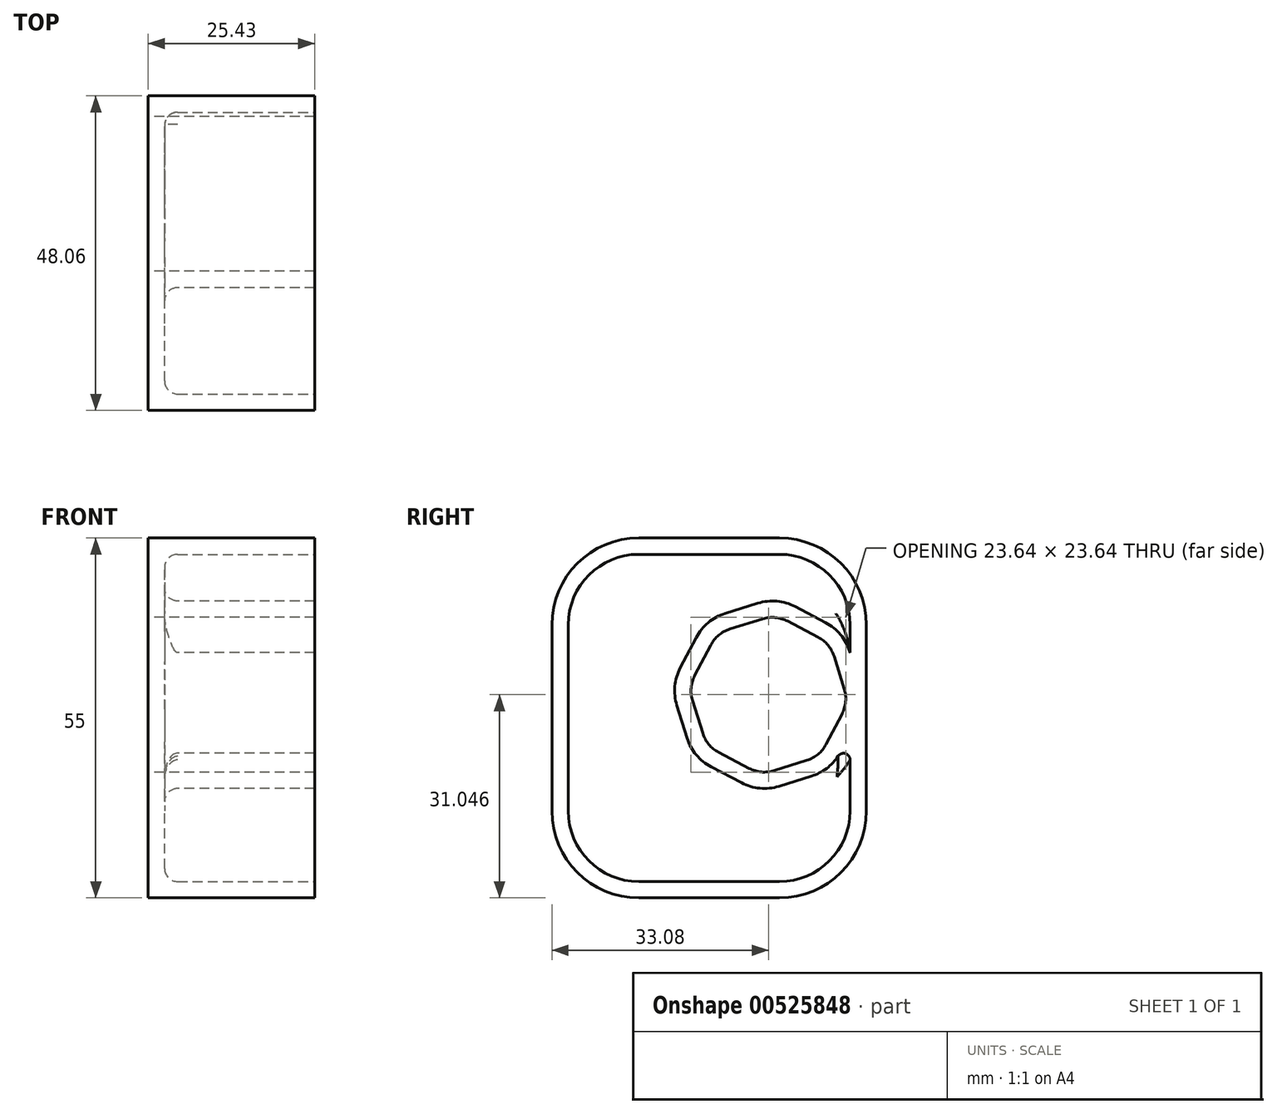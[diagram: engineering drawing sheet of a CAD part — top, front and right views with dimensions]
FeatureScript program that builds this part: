
annotation { "Feature Type Name" : "Feature", "Feature Type Description" : "" }
export const myFeature = defineFeature(function(context is Context, id is Id, definition is map)
    precondition{}
    {
        {
            var Q0;
            Q0=qCreatedBy(makeId("Top.planeOp"),FACE);
            var sketch = newSketch(context, id + "F0", { "sketchPlane" : qUnion([Q0])});
            skLineSegment(sketch, "E0.bottom", {"start": v(0, 0) * mm, "end": v(25.43, 0) * mm});
            skLineSegment(sketch, "E0.top", {"start": v(0, 48.06) * mm, "end": v(25.43, 48.06) * mm});
            skLineSegment(sketch, "E0.left", {"start": v(0, 0) * mm, "end": v(0, 48.06) * mm});
            skLineSegment(sketch, "E0.right", {"start": v(25.43, 0) * mm, "end": v(25.43, 48.06) * mm});
            skSolve(sketch);
        }
        {
            var Q0;
            Q0=makeQuery(id+"F0.imprint","IMPRINT",FACE,{"disambiguationData":[TD([[makeQuery(id+"F0.imprint","IMPRINT",EDGE,{"derivedFrom":sQuery(id+"F0.wireOp",EDGE,"E0.bottom")}),1.0]])]});
            extrude(context, id + "F1", {"entities" : qUnion([Q0]), "depth" : 55 * mm, "offsetDistance" : 25 * mm});
        }
        {
            var Q0;
            Q0=makeQuery(id+"F1.opExtrude","SWEPT_FACE",FACE,{"disambiguationData":[OSD([sQuery(id+"F0.wireOp",EDGE,"E0.right")])]});
            var sketch = newSketch(context, id + "F2", { "sketchPlane" : qUnion([Q0])});
            skCircle(sketch, "E1.cCircle", {"center": v(33.08, 31.05) * mm, "radius": 11.33 * mm, "construction": true});
            skLineSegment(sketch, "E1.0", {"start": v(40.93, 21.63) * mm, "end": v(31.97, 18.84) * mm});
            skLineSegment(sketch, "E1.1", {"start": v(31.97, 18.84) * mm, "end": v(23.66, 23.2) * mm});
            skLineSegment(sketch, "E1.2", {"start": v(23.66, 23.2) * mm, "end": v(20.87, 32.15) * mm});
            skLineSegment(sketch, "E1.3", {"start": v(20.87, 32.15) * mm, "end": v(25.23, 40.46) * mm});
            skLineSegment(sketch, "E1.4", {"start": v(25.23, 40.46) * mm, "end": v(34.19, 43.26) * mm});
            skLineSegment(sketch, "E1.5", {"start": v(34.19, 43.26) * mm, "end": v(42.5, 38.9) * mm});
            skLineSegment(sketch, "E1.6", {"start": v(42.5, 38.9) * mm, "end": v(45.29, 29.94) * mm});
            skLineSegment(sketch, "E1.7", {"start": v(45.29, 29.94) * mm, "end": v(40.93, 21.63) * mm});
            skPoint(sketch, "E1.0.midPoint", {"position": v(36.45, 20.23) * mm});
            skSolve(sketch);
        }
        {
            var Q0;
            Q0=makeQuery(id+"F2.imprint","IMPRINT",FACE,{"disambiguationData":[TD([[makeQuery(id+"F2.imprint","IMPRINT",EDGE,{"derivedFrom":sQuery(id+"F2.wireOp",EDGE,"E1.0")}),-1.0]])]});
            extrude(context, id + "F3", {"entities" : qUnion([Q0]), "operationType" : NewBodyOperationType.REMOVE, "oppositeDirection" : true, "depth" : 62.1 * mm, "offsetDistance" : 25 * mm});
        }
        {
            var Q0;
            Q0=makeQuery(id+"F1.opExtrude","CAP_EDGE",EDGE,{"disambiguationData":[OSD([sQuery(id+"F0.wireOp",EDGE,"E0.bottom")])],"isStart":false});
            var Q1;
            Q1=makeQuery(id+"F1.opExtrude","CAP_EDGE",EDGE,{"disambiguationData":[OSD([sQuery(id+"F0.wireOp",EDGE,"E0.bottom")])],"isStart":true});
            var Q2;
            Q2=makeQuery(id+"F1.opExtrude","CAP_EDGE",EDGE,{"disambiguationData":[OSD([sQuery(id+"F0.wireOp",EDGE,"E0.top")])],"isStart":false});
            var Q3;
            Q3=makeQuery(id+"F1.opExtrude","CAP_EDGE",EDGE,{"disambiguationData":[OSD([sQuery(id+"F0.wireOp",EDGE,"E0.top")])],"isStart":true});
            fillet(context, id + "F4", {"entities" : qUnion([Q0, Q1, Q2, Q3]), "radius" : 13.28 * mm, "tangentPropagation" : true, "allowEdgeOverflow" : false});
        }
        {
            var Q0;
            Q0=makeQuery(id+"F3.boolean.opBoolean","COPY",EDGE,{"derivedFrom":makeQuery(id+"F3.opExtrude","SWEPT_EDGE",EDGE,{"disambiguationData":[OSD([sQuery(id+"F2.wireOp",EDGE,"E1.4"),sQuery(id+"F2.wireOp",EDGE,"E1.5")])]})});
            var Q1;
            Q1=makeQuery(id+"F3.boolean.opBoolean","COPY",EDGE,{"derivedFrom":makeQuery(id+"F3.opExtrude","SWEPT_EDGE",EDGE,{"disambiguationData":[OSD([sQuery(id+"F2.wireOp",EDGE,"E1.5"),sQuery(id+"F2.wireOp",EDGE,"E1.6")])]})});
            var Q2;
            Q2=makeQuery(id+"F3.boolean.opBoolean","COPY",EDGE,{"derivedFrom":makeQuery(id+"F3.opExtrude","SWEPT_EDGE",EDGE,{"disambiguationData":[OSD([sQuery(id+"F2.wireOp",EDGE,"E1.6"),sQuery(id+"F2.wireOp",EDGE,"E1.7")])]})});
            var Q3;
            Q3=makeQuery(id+"F3.boolean.opBoolean","COPY",EDGE,{"derivedFrom":makeQuery(id+"F3.opExtrude","SWEPT_EDGE",EDGE,{"disambiguationData":[OSD([sQuery(id+"F2.wireOp",EDGE,"E1.0"),sQuery(id+"F2.wireOp",EDGE,"E1.7")])]})});
            var Q4;
            Q4=makeQuery(id+"F3.boolean.opBoolean","COPY",EDGE,{"derivedFrom":makeQuery(id+"F3.opExtrude","SWEPT_EDGE",EDGE,{"disambiguationData":[OSD([sQuery(id+"F2.wireOp",EDGE,"E1.0"),sQuery(id+"F2.wireOp",EDGE,"E1.1")])]})});
            var Q5;
            Q5=makeQuery(id+"F3.boolean.opBoolean","COPY",EDGE,{"derivedFrom":makeQuery(id+"F3.opExtrude","SWEPT_EDGE",EDGE,{"disambiguationData":[OSD([sQuery(id+"F2.wireOp",EDGE,"E1.1"),sQuery(id+"F2.wireOp",EDGE,"E1.2")])]})});
            var Q6;
            Q6=makeQuery(id+"F3.boolean.opBoolean","COPY",EDGE,{"derivedFrom":makeQuery(id+"F3.opExtrude","SWEPT_EDGE",EDGE,{"disambiguationData":[OSD([sQuery(id+"F2.wireOp",EDGE,"E1.2"),sQuery(id+"F2.wireOp",EDGE,"E1.3")])]})});
            var Q7;
            Q7=makeQuery(id+"F3.boolean.opBoolean","COPY",EDGE,{"derivedFrom":makeQuery(id+"F3.opExtrude","SWEPT_EDGE",EDGE,{"disambiguationData":[OSD([sQuery(id+"F2.wireOp",EDGE,"E1.3"),sQuery(id+"F2.wireOp",EDGE,"E1.4")])]})});
            fillet(context, id + "F5", {"entities" : qUnion([Q0, Q1, Q2, Q3, Q4, Q5, Q6, Q7]), "radius" : 5 * mm, "tangentPropagation" : true, "allowEdgeOverflow" : false});
        }
        {
            var Q0;
            Q0=makeQuery(id+"F1.opExtrude","SWEPT_FACE",FACE,{"disambiguationData":[OSD([sQuery(id+"F0.wireOp",EDGE,"E0.right")])]});
            shell(context, id + "F6", {"entities" : qUnion([Q0]), "thickness" : 2.5 * mm});
        }
        {
            var Q0;
            Q0=makeQuery(id+"F6.opShell","TWEAK_EDGE",EDGE,{"derivedFrom":[makeQuery(id+"F1.opExtrude","SWEPT_FACE",FACE,{"disambiguationData":[OSD([sQuery(id+"F0.wireOp",EDGE,"E0.top")])]}),makeQuery(id+"F3.boolean.opBoolean","COPY",FACE,{"derivedFrom":makeQuery(id+"F3.opExtrude","SWEPT_FACE",FACE,{"disambiguationData":[OSD([sQuery(id+"F2.wireOp",EDGE,"E1.7")])]})})]});
            fillet(context, id + "F7", {"entities" : qUnion([Q0]), "radius" : 1 * mm, "tangentPropagation" : true, "allowEdgeOverflow" : false});
        }
        {
            var Q0;
            Q0=makeQuery(id+"F6.opShell","OFFSET_FACE",FACE,{"disambiguationData":[OSD([sQuery(id+"F0.wireOp",EDGE,"E0.left")])]});
            fillet(context, id + "F8", {"entities" : qUnion([Q0]), "radius" : 2 * mm, "tangentPropagation" : true, "allowEdgeOverflow" : false});
        }
    });
